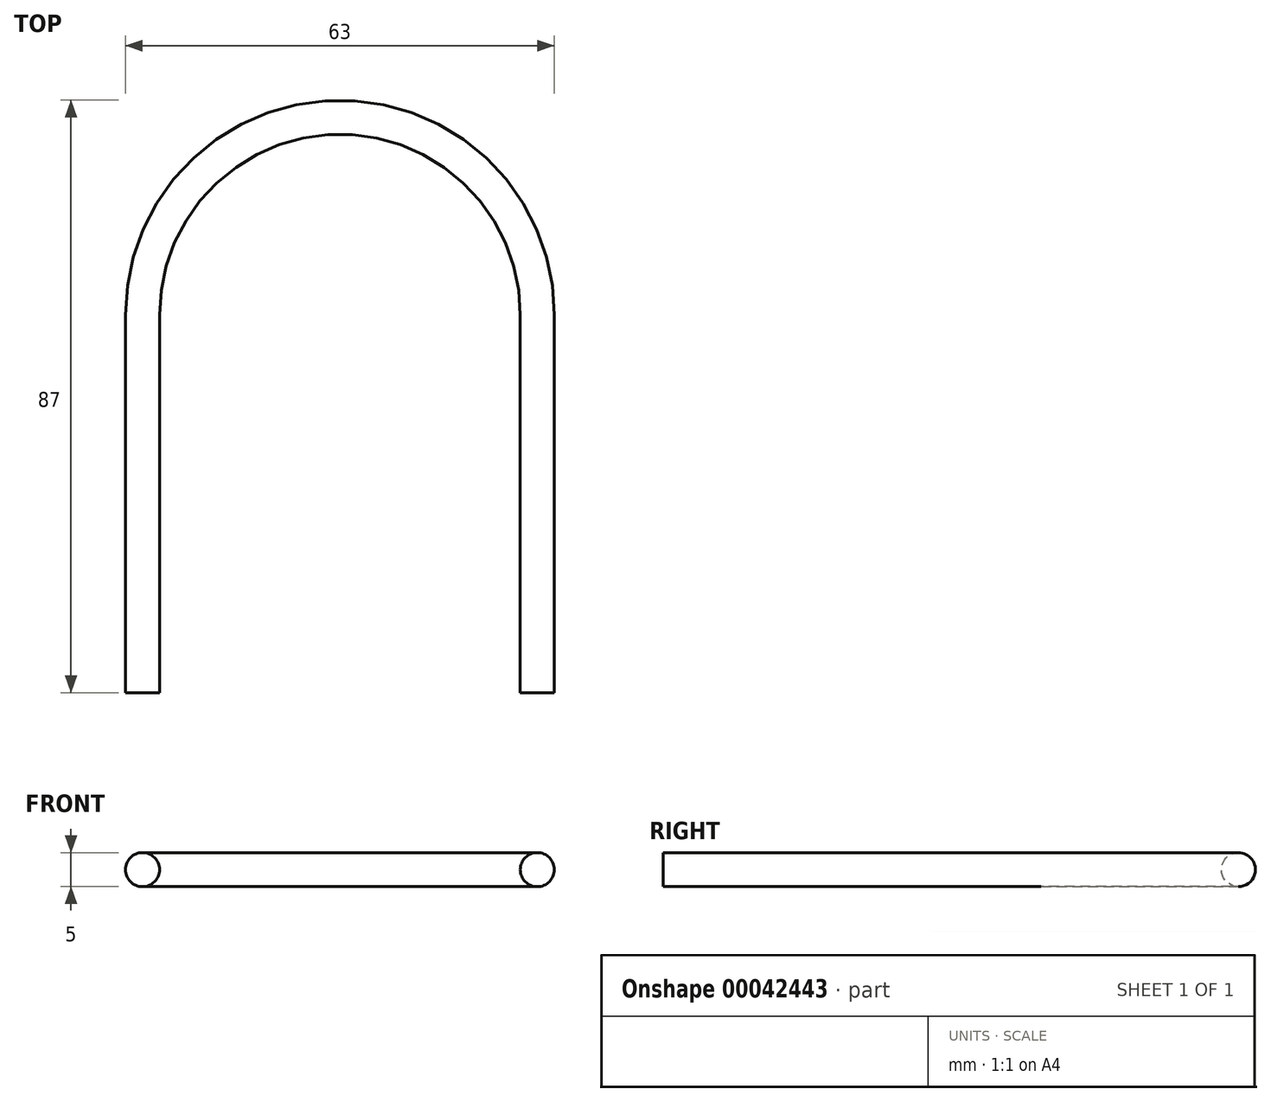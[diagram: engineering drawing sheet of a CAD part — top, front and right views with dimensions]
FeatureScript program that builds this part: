
annotation { "Feature Type Name" : "Feature", "Feature Type Description" : "" }
export const myFeature = defineFeature(function(context is Context, id is Id, definition is map)
    precondition{}
    {
        {
            var Q0;
            Q0=qCreatedBy(makeId("Top.planeOp"),FACE);
            var sketch = newSketch(context, id + "F0", { "sketchPlane" : qUnion([Q0])});
            skLineSegment(sketch, "E0.bottom", {"start": v(0, 0) * mm, "end": v(75, 0) * mm, "construction": true});
            skLineSegment(sketch, "E0.top", {"start": v(0, 85) * mm, "end": v(75, 85) * mm, "construction": true});
            skLineSegment(sketch, "E0.left", {"start": v(0, 0) * mm, "end": v(0, 85) * mm, "construction": true});
            skLineSegment(sketch, "E0.right", {"start": v(75, 0) * mm, "end": v(75, 85) * mm, "construction": true});
            skLineSegment(sketch, "E1", {"start": v(37.5, 85) * mm, "end": v(37.5, 0) * mm, "construction": true});
            skCircle(sketch, "E2", {"center": v(37.5, 47.5) * mm, "radius": 31.5 * mm, "construction": true});
            skLineSegment(sketch, "E3", {"start": v(37.5, 79) * mm, "end": v(37.5, 85) * mm, "construction": true});
            skLineSegment(sketch, "E4", {"start": v(6, 47.5) * mm, "end": v(0, 47.5) * mm, "construction": true});
            skArc(sketch, "E5", {"start": v(69, 47.5) * mm, "mid": v(37.5, 79) * mm, "end": v(6, 47.5) * mm});
            skLineSegment(sketch, "E6", {"start": v(6, 47.5) * mm, "end": v(6, -8) * mm});
            skLineSegment(sketch, "E7", {"start": v(6, -8) * mm, "end": v(11, -8) * mm});
            skLineSegment(sketch, "E8", {"start": v(11, -8) * mm, "end": v(11, 47.5) * mm});
            skLineSegment(sketch, "E9.0.MirrorCS", {"start": v(69, 47.5) * mm, "end": v(69, -8) * mm});
            skLineSegment(sketch, "E9.1.MirrorCS", {"start": v(64, -8) * mm, "end": v(64, 47.5) * mm});
            skLineSegment(sketch, "E9.2.MirrorCS", {"start": v(69, -8) * mm, "end": v(64, -8) * mm});
            skArc(sketch, "E10", {"start": v(64, 47.5) * mm, "mid": v(37.5, 74) * mm, "end": v(11, 47.5) * mm});
            skSolve(sketch);
        }
        {
            var Q0;
            Q0=qSketchRegion(id+"F0",true);
            extrude(context, id + "F1", {"entities" : qUnion([Q0]), "depth" : 5 * mm});
        }
        {
            var Q0;
            Q0=makeQuery(id+"F1.opExtrude","CAP_EDGE",EDGE,{"disambiguationData":[OSD([sQuery(id+"F0.wireOp",EDGE,"E5")])],"isStart":false});
            var Q1;
            Q1=makeQuery(id+"F1.opExtrude","CAP_EDGE",EDGE,{"disambiguationData":[OSD([sQuery(id+"F0.wireOp",EDGE,"E10")])],"isStart":false});
            var Q2;
            Q2=makeQuery(id+"F1.opExtrude","CAP_EDGE",EDGE,{"disambiguationData":[OSD([sQuery(id+"F0.wireOp",EDGE,"E6")])],"isStart":true});
            var Q3;
            Q3=makeQuery(id+"F1.opExtrude","CAP_EDGE",EDGE,{"disambiguationData":[OSD([sQuery(id+"F0.wireOp",EDGE,"E8")])],"isStart":true});
            fillet(context, id + "F2", {"entities" : qUnion([Q0, Q1, Q2, Q3]), "radius" : 2.5 * mm, "tangentPropagation" : true, "allowEdgeOverflow" : false});
        }
    });
